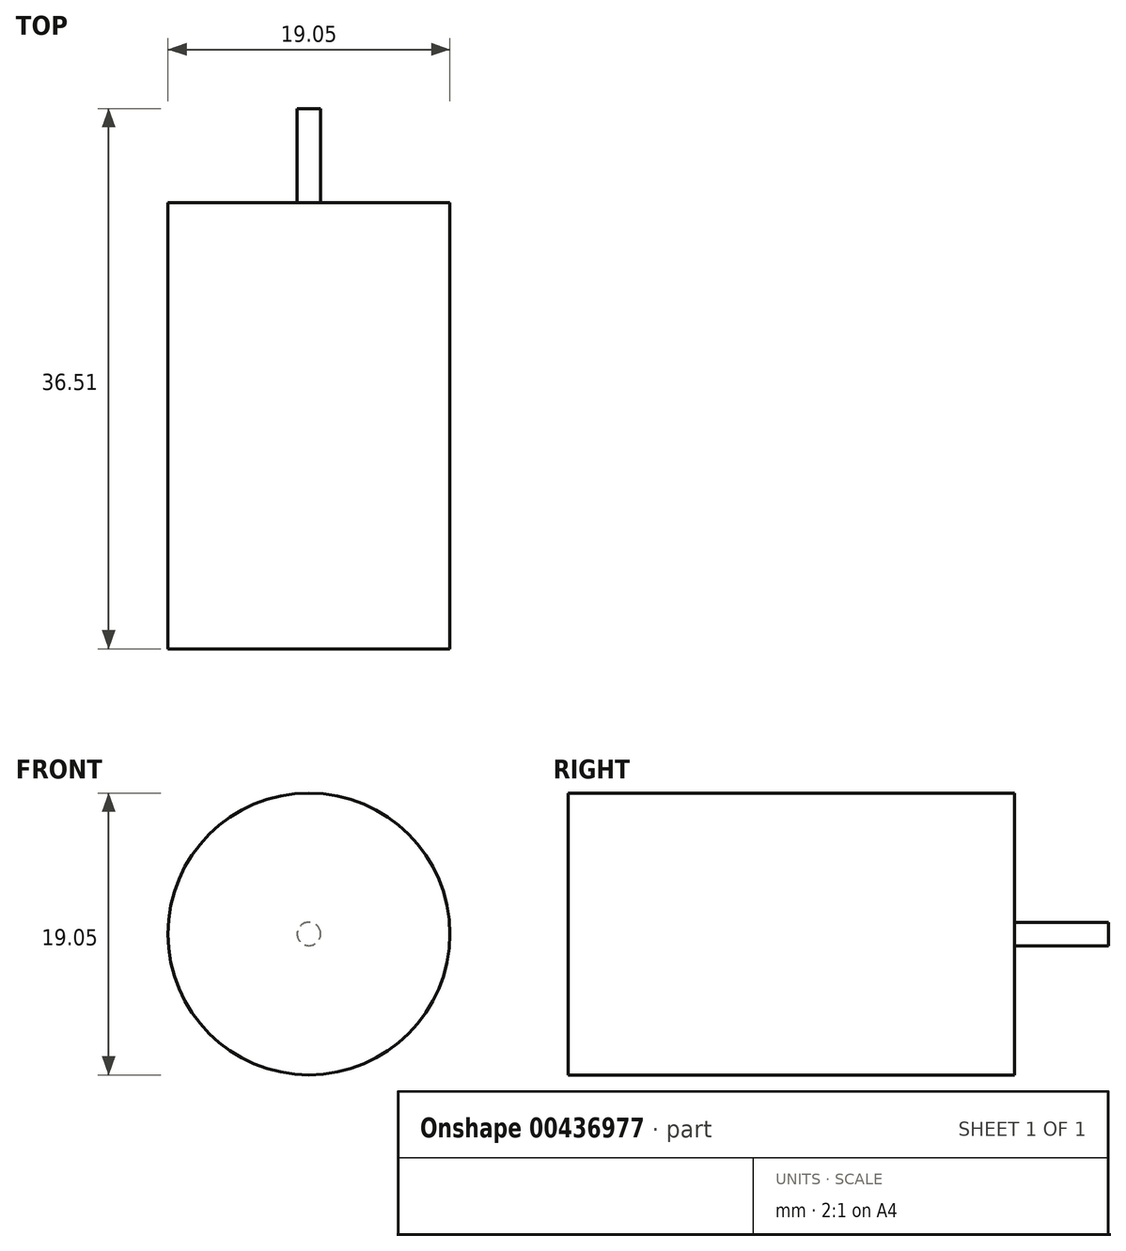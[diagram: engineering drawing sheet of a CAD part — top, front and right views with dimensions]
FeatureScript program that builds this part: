
annotation { "Feature Type Name" : "Feature", "Feature Type Description" : "" }
export const myFeature = defineFeature(function(context is Context, id is Id, definition is map)
    precondition{}
    {
        {
            var Q0;
            Q0=qCreatedBy(makeId("Front.planeOp"),FACE);
            var sketch = newSketch(context, id + "F0", { "sketchPlane" : qUnion([Q0])});
            skCircle(sketch, "E0", {"center": v(-110.8, 17.8) * mm, "radius": 9.53 * mm});
            skSolve(sketch);
        }
        {
            var Q0;
            Q0=makeQuery(id+"F0.imprint","IMPRINT",FACE,{"disambiguationData":[TD([[makeQuery(id+"F0.imprint","IMPRINT",EDGE,{"derivedFrom":sQuery(id+"F0.wireOp",EDGE,"E0")}),1.0]])]});
            extrude(context, id + "F1", {"entities" : qUnion([Q0]), "depth" : 30.16 * mm});
        }
        {
            var Q0;
            Q0=makeQuery(id+"F1.opExtrude","CAP_FACE",FACE,{"disambiguationData":[OSD([sQuery(id+"F0.wireOp",EDGE,"E0")])],"isStart":true});
            var sketch = newSketch(context, id + "F2", { "sketchPlane" : qUnion([Q0])});
            skCircle(sketch, "E1", {"center": v(110.8, 17.8) * mm, "radius": 0.8 * mm});
            skSolve(sketch);
        }
        {
            var Q0;
            Q0 = qSketchRegion(id + "F2", true);
            extrude(context, id + "F3", {"entities" : qUnion([Q0]), "operationType" : NewBodyOperationType.ADD, "depth" : 6.35 * mm});
        }
    });
